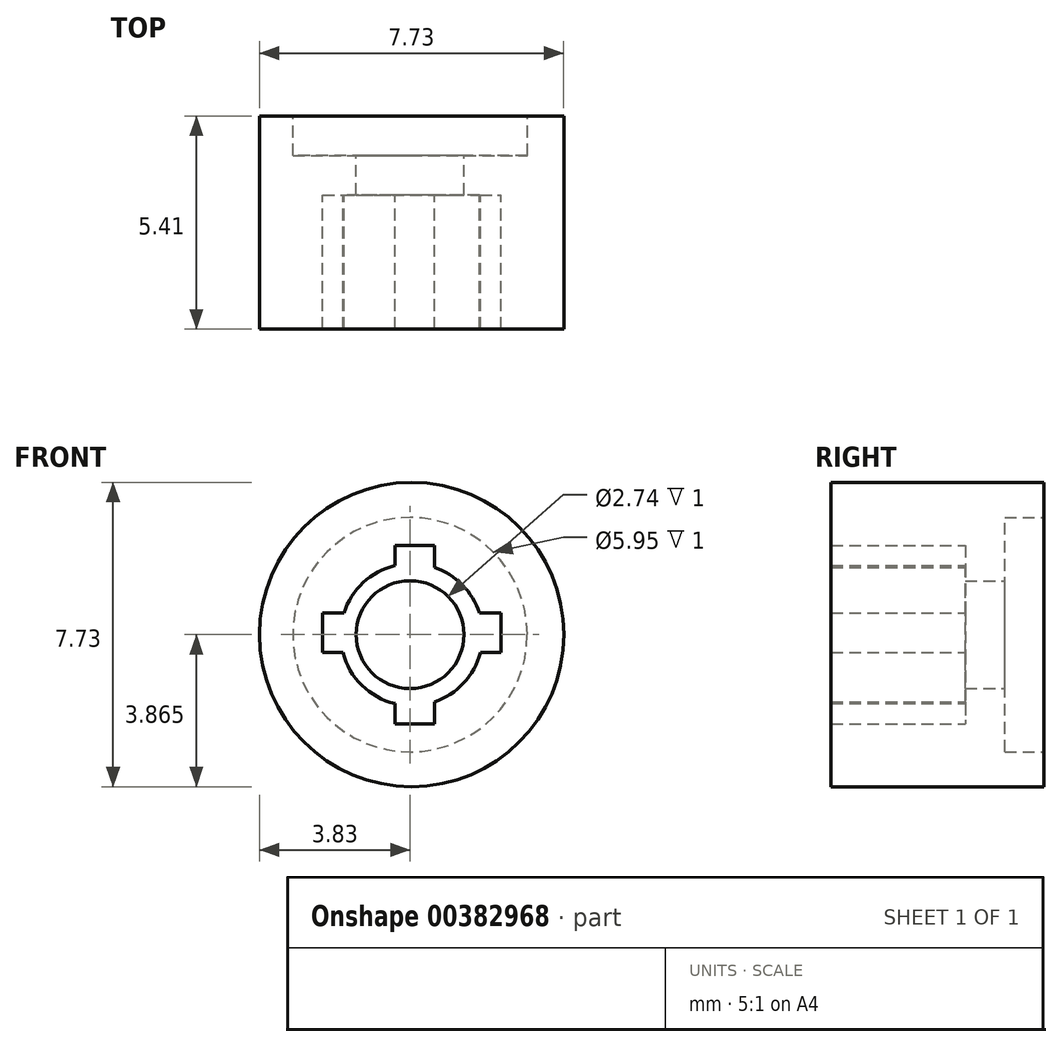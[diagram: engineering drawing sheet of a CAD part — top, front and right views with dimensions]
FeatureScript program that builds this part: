
annotation { "Feature Type Name" : "Feature", "Feature Type Description" : "" }
export const myFeature = defineFeature(function(context is Context, id is Id, definition is map)
    precondition{}
    {
        {
            var Q0;
            Q0=qCreatedBy(makeId("Front.planeOp"),FACE);
            var sketch = newSketch(context, id + "F0", { "sketchPlane" : qUnion([Q0])});
            skCircle(sketch, "E0", {"center": v(30.72, 18.94) * mm, "radius": 3.87 * mm});
            skArc(sketch, "E1", {"start": v(30.3, 20.7) * mm, "mid": v(29.49, 20.26) * mm, "end": v(29, 19.48) * mm});
            skLineSegment(sketch, "E2.bottom", {"start": v(31.3, 21.2) * mm, "end": v(30.3, 21.2) * mm});
            skLineSegment(sketch, "E2.top", {"start": v(31.3, 16.67) * mm, "end": v(30.3, 16.67) * mm});
            skLineSegment(sketch, "E2.left", {"start": v(31.3, 21.2) * mm, "end": v(31.3, 20.65) * mm});
            skLineSegment(sketch, "E2.right", {"start": v(30.3, 21.2) * mm, "end": v(30.3, 20.7) * mm});
            skLineSegment(sketch, "E3.bottom", {"start": v(28.45, 19.48) * mm, "end": v(29, 19.48) * mm});
            skLineSegment(sketch, "E3.top", {"start": v(28.45, 18.48) * mm, "end": v(28.97, 18.48) * mm});
            skLineSegment(sketch, "E3.left", {"start": v(28.45, 19.48) * mm, "end": v(28.45, 18.48) * mm});
            skLineSegment(sketch, "E3.right", {"start": v(32.98, 19.48) * mm, "end": v(32.98, 18.48) * mm});
            skArc(sketch, "E4.trimOffspring", {"start": v(32.44, 19.48) * mm, "mid": v(32, 20.2) * mm, "end": v(31.3, 20.65) * mm});
            skLineSegment(sketch, "E5.trimOffspring", {"start": v(32.44, 19.48) * mm, "end": v(32.98, 19.48) * mm});
            skLineSegment(sketch, "E6.trimOffspring", {"start": v(30.3, 17.18) * mm, "end": v(30.3, 16.67) * mm});
            skLineSegment(sketch, "E7.trimOffspring", {"start": v(31.3, 17.23) * mm, "end": v(31.3, 16.67) * mm});
            skLineSegment(sketch, "E8.trimOffspring", {"start": v(32.47, 18.48) * mm, "end": v(32.98, 18.48) * mm});
            skArc(sketch, "E9.trimOffspring", {"start": v(28.97, 18.48) * mm, "mid": v(29.46, 17.65) * mm, "end": v(30.3, 17.18) * mm});
            skArc(sketch, "E10.trimOffspring", {"start": v(31.3, 17.23) * mm, "mid": v(32.04, 17.7) * mm, "end": v(32.47, 18.48) * mm});
            skSolve(sketch);
        }
        {
            var Q0;
            Q0=makeQuery(id+"F0.imprint","IMPRINT",FACE,{"disambiguationData":[TD([[makeQuery(id+"F0.imprint","IMPRINT",EDGE,{"derivedFrom":sQuery(id+"F0.wireOp",EDGE,"E0")}),1.0]])]});
            extrude(context, id + "F1", {"entities" : qUnion([Q0]), "depth" : 5.4 * mm});
        }
        {
            var Q0;
            Q0=qCreatedBy(makeId("Front.planeOp"),FACE);
            var sketch = newSketch(context, id + "F2", { "sketchPlane" : qUnion([Q0])});
            skCircle(sketch, "E11", {"center": v(30.68, 18.94) * mm, "radius": 1.37 * mm});
            skCircle(sketch, "E12", {"center": v(30.68, 18.94) * mm, "radius": 2.98 * mm});
            skSolve(sketch);
        }
        {
            var Q0;
            Q0=makeQuery(id+"F2.imprint","IMPRINT",FACE,{"disambiguationData":[TD([[makeQuery(id+"F2.imprint","IMPRINT",EDGE,{"derivedFrom":sQuery(id+"F2.wireOp",EDGE,"E11")}),-1.0]])]});
            extrude(context, id + "F3", {"entities" : qUnion([Q0]), "operationType" : NewBodyOperationType.ADD, "depth" : 2 * mm});
        }
        {
            var Q0;
            Q0=makeQuery(id+"F2.imprint","IMPRINT",FACE,{"disambiguationData":[TD([[makeQuery(id+"F2.imprint","IMPRINT",EDGE,{"derivedFrom":sQuery(id+"F2.wireOp",EDGE,"E11")}),-1.0]])]});
            extrude(context, id + "F4", {"entities" : qUnion([Q0]), "operationType" : NewBodyOperationType.REMOVE, "depth" : 1 * mm});
        }
    });
